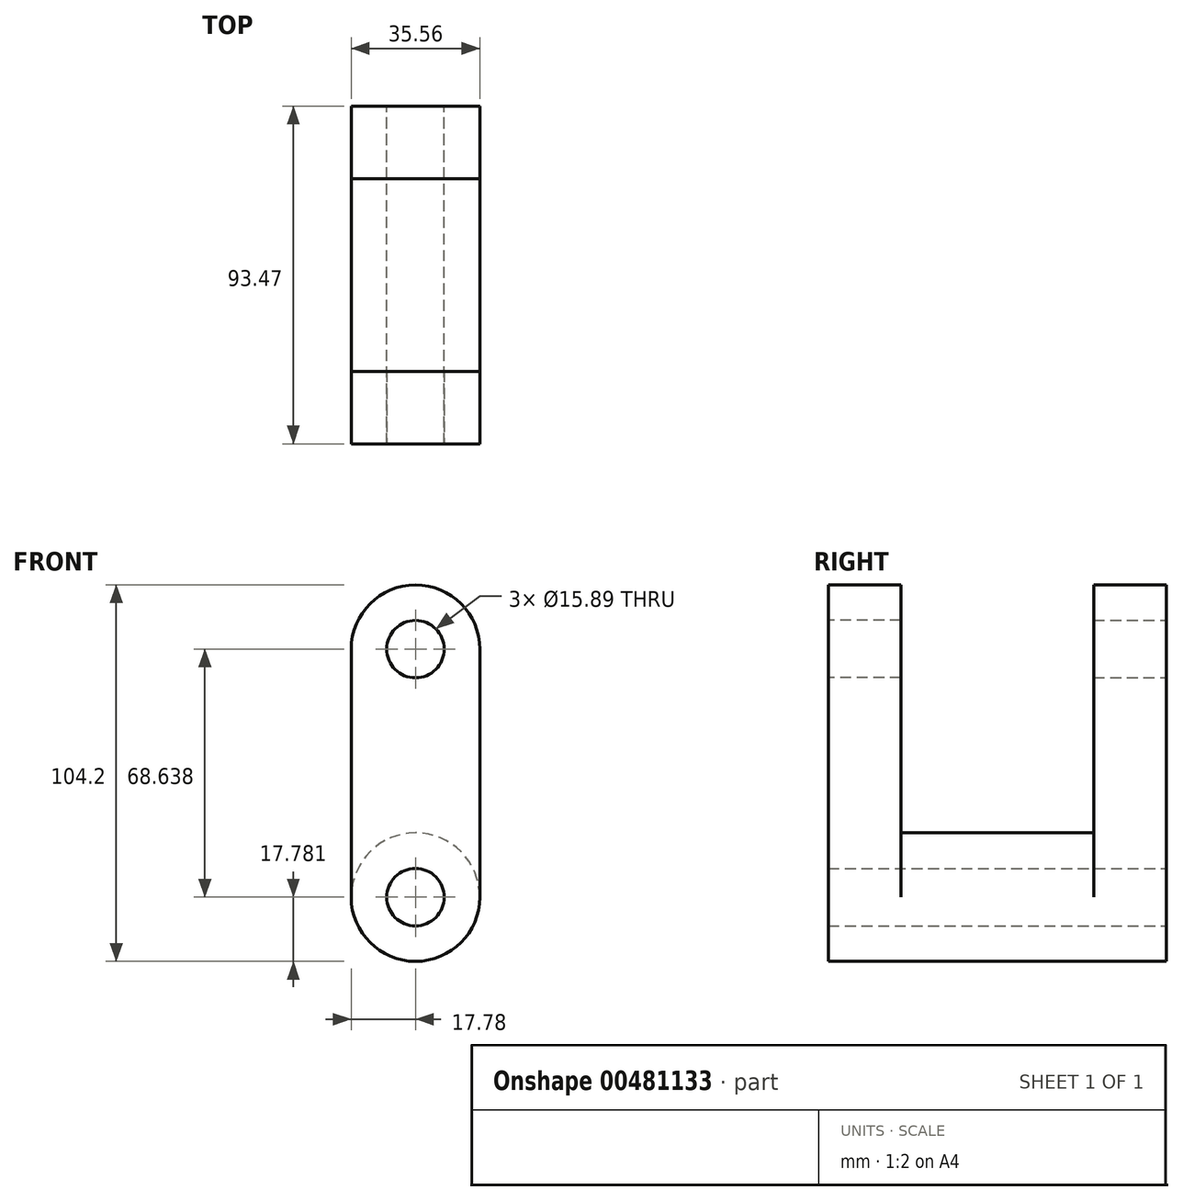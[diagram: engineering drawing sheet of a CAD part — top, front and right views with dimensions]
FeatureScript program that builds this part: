
annotation { "Feature Type Name" : "Feature", "Feature Type Description" : "" }
export const myFeature = defineFeature(function(context is Context, id is Id, definition is map)
    precondition{}
    {
        {
            var Q0;
            Q0=qCreatedBy(makeId("Front.planeOp"),FACE);
            var sketch = newSketch(context, id + "F0", { "sketchPlane" : qUnion([Q0])});
            skCircle(sketch, "E0", {"center": v(0, 34.32) * mm, "radius": 7.94 * mm});
            skCircle(sketch, "E1", {"center": v(0, -34.32) * mm, "radius": 7.94 * mm});
            skArc(sketch, "E2", {"start": v(17.78, 34.32) * mm, "mid": v(0, 52.1) * mm, "end": v(-17.78, 34.32) * mm});
            skCircle(sketch, "E3", {"center": v(0, -34.32) * mm, "radius": 17.78 * mm});
            skLineSegment(sketch, "E4", {"start": v(-17.78, 34.32) * mm, "end": v(-17.78, -34.32) * mm});
            skLineSegment(sketch, "E5", {"start": v(17.78, 34.32) * mm, "end": v(17.78, -34.32) * mm});
            skSolve(sketch);
        }
        {
            var Q0;
            Q0 = qSketchRegion(id + "F0", true);
            extrude(context, id + "F1", {"entities" : qUnion([Q0]), "depth" : 20.07 * mm});
        }
        {
            var Q0;
            Q0=makeQuery(id+"F0.imprint","IMPRINT",FACE,{"disambiguationData":[TD([[makeQuery(id+"F0.imprint","IMPRINT",EDGE,{"derivedFrom":sQuery(id+"F0.wireOp",EDGE,"E1")}),-1.0]])]});
            extrude(context, id + "F2", {"entities" : qUnion([Q0]), "operationType" : NewBodyOperationType.ADD, "depth" : 46.74 * mm});
        }
        {
            var Q0;
            Q0=makeQuery(id+"F2.opExtrude","CAP_FACE",FACE,{"disambiguationData":[OSD([sQuery(id+"F0.wireOp",EDGE,"E1"),sQuery(id+"F0.wireOp",EDGE,"E3")])],"isStart":false});
            cPlane(context, id + "F3", {"entities" : qUnion([Q0]), "cplaneType" : CPlaneType.OFFSET, "offset" : 0 * mm, "width" : 152.4 * mm, "height" : 152.4 * mm});
        }
        {
            var Q0;
            Q0=makeQuery(id+"F1.opExtrude","SWEPT_BODY",BODY,{"disambiguationData":[OSD([sQuery(id+"F0.wireOp",EDGE,"E0"),sQuery(id+"F0.wireOp",EDGE,"E1"),sQuery(id+"F0.wireOp",EDGE,"E2"),sQuery(id+"F0.wireOp",EDGE,"E3"),sQuery(id+"F0.wireOp",EDGE,"E4"),sQuery(id+"F0.wireOp",EDGE,"E5")])]});
            var Q1;
            Q1=qCreatedBy(id+"F3.planeOp",FACE);
            mirror(context, id + "F4", {"operationType" : NewBodyOperationType.ADD, "entities" : qUnion([Q0]), "mirrorPlane" : qUnion([Q1])});
        }
    });
